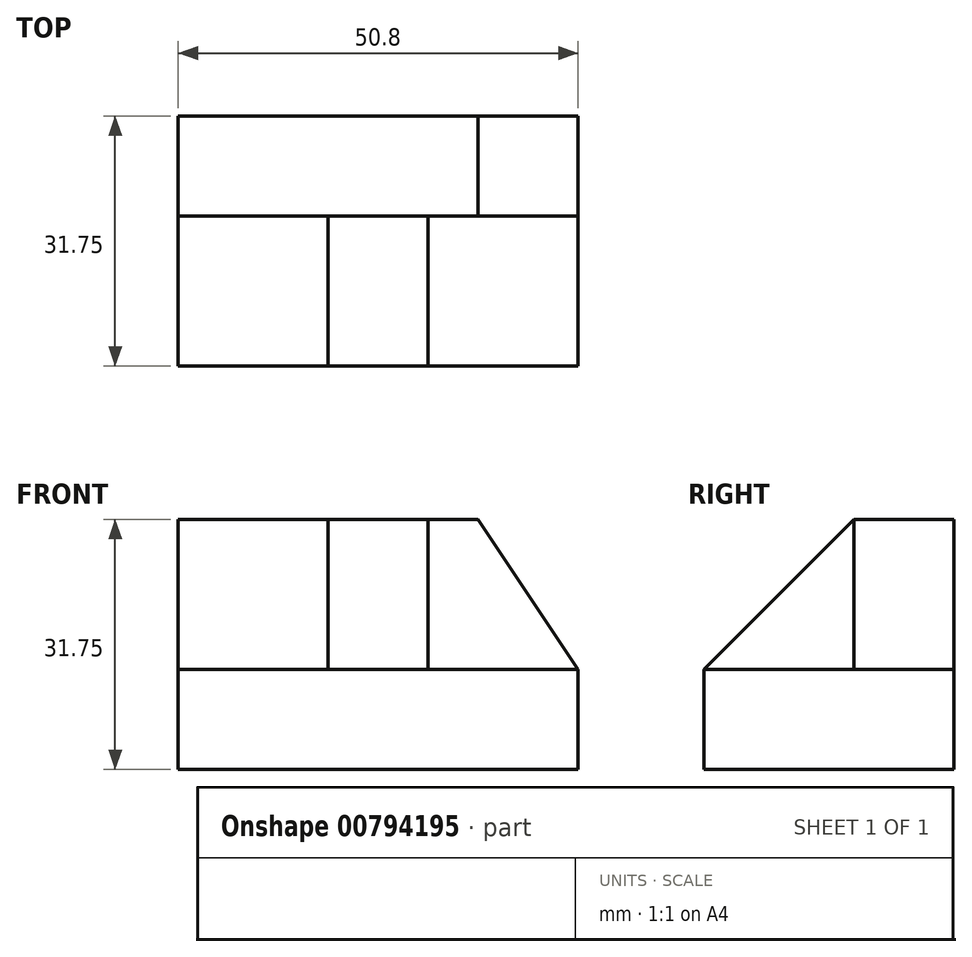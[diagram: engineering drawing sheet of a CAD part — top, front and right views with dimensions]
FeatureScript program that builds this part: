
annotation { "Feature Type Name" : "Feature", "Feature Type Description" : "" }
export const myFeature = defineFeature(function(context is Context, id is Id, definition is map)
    precondition{}
    {
        {
            var Q0;
            Q0=qCreatedBy(makeId("Front.planeOp"),FACE);
            var sketch = newSketch(context, id + "F0", { "sketchPlane" : qUnion([Q0])});
            skLineSegment(sketch, "E0", {"start": v(0, 0) * mm, "end": v(50.8, 0) * mm});
            skLineSegment(sketch, "E1", {"start": v(0, 0) * mm, "end": v(0, 31.75) * mm});
            skLineSegment(sketch, "E2", {"start": v(0, 31.75) * mm, "end": v(50.8, 31.75) * mm});
            skLineSegment(sketch, "E3", {"start": v(50.8, 31.75) * mm, "end": v(50.8, 0) * mm});
            skSolve(sketch);
        }
        {
            var Q0;
            Q0=makeQuery(id+"F0.imprint","IMPRINT",FACE,{"disambiguationData":[TD([[makeQuery(id+"F0.imprint","IMPRINT",EDGE,{"derivedFrom":sQuery(id+"F0.wireOp",EDGE,"E0")}),1.0]])]});
            extrude(context, id + "F1", {"entities" : qUnion([Q0]), "depth" : 31.75 * mm, "offsetDistance" : 25.4 * mm});
        }
        {
            var Q0;
            Q0=makeQuery(id+"F1.opExtrude","SWEPT_FACE",FACE,{"disambiguationData":[OSD([sQuery(id+"F0.wireOp",EDGE,"E3")])]});
            var sketch = newSketch(context, id + "F2", { "sketchPlane" : qUnion([Q0])});
            skLineSegment(sketch, "E4", {"start": v(-12.7, 31.75) * mm, "end": v(-12.7, 12.7) * mm});
            skLineSegment(sketch, "E5", {"start": v(-12.7, 12.7) * mm, "end": v(-31.75, 12.7) * mm});
            skSolve(sketch);
        }
        {
            var Q0;
            {var subQ0=sQuery(id+"F2.wireOp",EDGE,"E4");Q0=makeQuery(id+"F2.imprint","IMPRINT",FACE,{"disambiguationData":[TD([[makeQuery(id+"F2.imprint","IMPRINT",EDGE,{"derivedFrom":subQ0}),-1.0]])]});}
            extrude(context, id + "F3", {"entities" : qUnion([Q0]), "operationType" : NewBodyOperationType.REMOVE, "oppositeDirection" : true, "depth" : 19.05 * mm, "offsetDistance" : 25.4 * mm});
        }
        {
            var Q0;
            Q0=makeQuery(id+"F3.boolean.opBoolean","COPY",FACE,{"derivedFrom":makeQuery(id+"F3.opExtrude","SWEPT_FACE",FACE,{"disambiguationData":[OSD([sQuery(id+"F2.wireOp",EDGE,"E4")])]})});
            var sketch = newSketch(context, id + "F4", { "sketchPlane" : qUnion([Q0])});
            skLineSegment(sketch, "E6", {"start": v(31.75, 31.75) * mm, "end": v(38.1, 31.75) * mm, "construction": true});
            skLineSegment(sketch, "E7", {"start": v(38.1, 31.75) * mm, "end": v(50.8, 12.7) * mm});
            skSolve(sketch);
        }
        {
            var Q0;
            {var subQ0=sQuery(id+"F4.wireOp",EDGE,"E7");Q0=makeQuery(id+"F4.imprint","IMPRINT",FACE,{"disambiguationData":[TD([[makeQuery(id+"F4.imprint","IMPRINT",EDGE,{"derivedFrom":subQ0}),1.0]])]});}
            extrude(context, id + "F5", {"entities" : qUnion([Q0]), "operationType" : NewBodyOperationType.REMOVE, "endBound" : BoundingType.THROUGH_ALL, "oppositeDirection" : true, "depth" : 25.4 * mm, "offsetDistance" : 25.4 * mm});
        }
        {
            var Q0;
            Q0=makeQuery(id+"F3.boolean.opBoolean","COPY",FACE,{"derivedFrom":makeQuery(id+"F3.opExtrude","CAP_FACE",FACE,{"disambiguationData":[OSD([sQuery(id+"F0.wireOp",EDGE,"E2"),sQuery(id+"F0.wireOp",EDGE,"E3"),sQuery(id+"F2.wireOp",EDGE,"E4"),sQuery(id+"F2.wireOp",EDGE,"E5")])],"isStart":false})});
            var sketch = newSketch(context, id + "F6", { "sketchPlane" : qUnion([Q0])});
            skLineSegment(sketch, "E8", {"start": v(-12.7, 31.75) * mm, "end": v(-31.75, 12.7) * mm});
            skLineSegment(sketch, "E9", {"start": v(-31.75, 12.7) * mm, "end": v(-31.75, 31.75) * mm});
            skLineSegment(sketch, "E10", {"start": v(-31.75, 31.75) * mm, "end": v(-12.7, 31.75) * mm});
            skSolve(sketch);
        }
        {
            var Q0;
            Q0=makeQuery(id+"F6.imprint","IMPRINT",FACE,{"disambiguationData":[TD([[makeQuery(id+"F6.imprint","IMPRINT",EDGE,{"derivedFrom":sQuery(id+"F6.wireOp",EDGE,"E8")}),-1.0]])]});
            extrude(context, id + "F7", {"entities" : qUnion([Q0]), "operationType" : NewBodyOperationType.REMOVE, "oppositeDirection" : true, "depth" : 12.7 * mm, "offsetDistance" : 25.4 * mm});
        }
        {
            var Q0;
            Q0=makeQuery(id+"F1.opExtrude","SWEPT_FACE",FACE,{"disambiguationData":[OSD([sQuery(id+"F0.wireOp",EDGE,"E1")])]});
            var sketch = newSketch(context, id + "F8", { "sketchPlane" : qUnion([Q0])});
            skLineSegment(sketch, "E11", {"start": v(0, 31.75) * mm, "end": v(12.7, 31.75) * mm, "construction": true});
            skLineSegment(sketch, "E12", {"start": v(12.7, 31.75) * mm, "end": v(12.7, 12.7) * mm});
            skLineSegment(sketch, "E13", {"start": v(12.7, 12.7) * mm, "end": v(31.75, 12.7) * mm});
            skSolve(sketch);
        }
        {
            var Q0;
            {var subQ0=sQuery(id+"F8.wireOp",EDGE,"E12");Q0=makeQuery(id+"F8.imprint","IMPRINT",FACE,{"disambiguationData":[TD([[makeQuery(id+"F8.imprint","IMPRINT",EDGE,{"derivedFrom":subQ0}),1.0]])]});}
            extrude(context, id + "F9", {"entities" : qUnion([Q0]), "operationType" : NewBodyOperationType.REMOVE, "oppositeDirection" : true, "depth" : 19.05 * mm, "offsetDistance" : 25.4 * mm});
        }
    });
